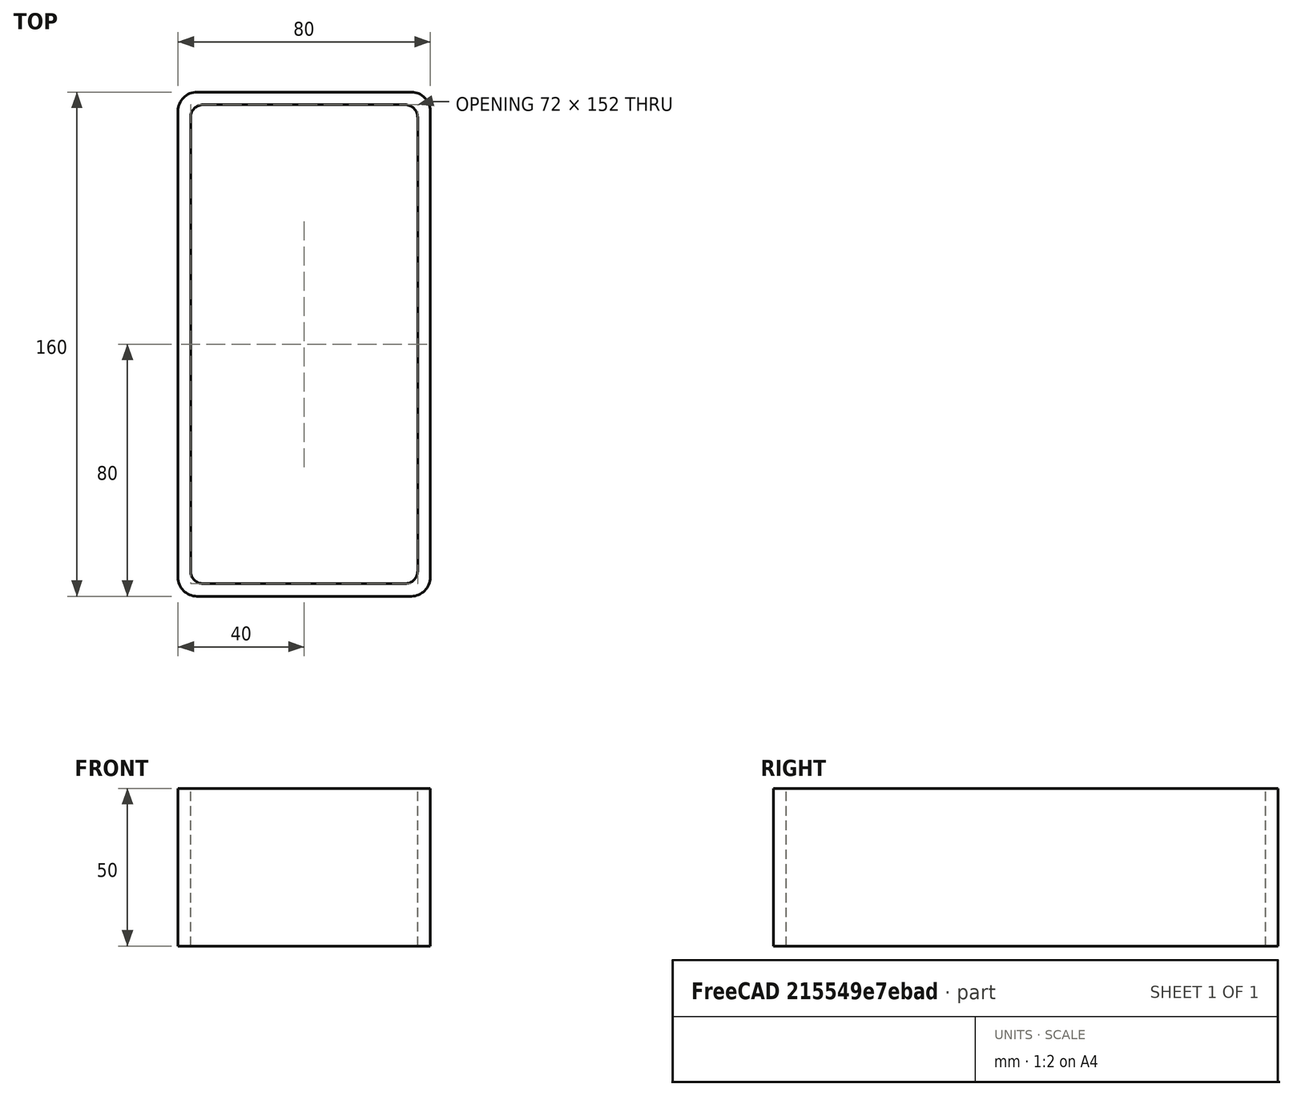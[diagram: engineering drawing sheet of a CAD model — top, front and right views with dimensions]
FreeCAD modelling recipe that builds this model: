
FCSTD DOCUMENT  (FreeCAD 0.15R4671 (Git))
Label: Rectangular hollow section 160x80x4 EN10219 S235JRH
License: All rights reserved
LicenseURL: http://en.wikipedia.org/wiki/All_rights_reserved
objects: Sketcher::SketchObject×1, Part::Extrusion×1
note: 2 computed .brp shape members not serialized (recipe doc carries the construction recipe); baked Part::Feature solids carry a one-line shape summary decoded from their .brp

FEATURE [Sketcher::SketchObject] Sketch
  sketch-geometry (16):
    g0: LineSegment StartX=-32 StartY=76 StartZ=0 EndX=32 EndY=76 EndZ=0
    g1: LineSegment StartX=36 StartY=72 StartZ=0 EndX=36 EndY=-72 EndZ=0
    g2: LineSegment StartX=32 StartY=-76 StartZ=0 EndX=-32 EndY=-76 EndZ=0
    g3: LineSegment StartX=-36 StartY=-72 StartZ=0 EndX=-36 EndY=72 EndZ=0
    g4: LineSegment StartX=-34 StartY=80 StartZ=0 EndX=34 EndY=80 EndZ=0
    g5: LineSegment StartX=40 StartY=74 StartZ=0 EndX=40 EndY=-74 EndZ=0
    g6: LineSegment StartX=34 StartY=-80 StartZ=0 EndX=-34 EndY=-80 EndZ=0
    g7: LineSegment StartX=-40 StartY=-74 StartZ=0 EndX=-40 EndY=74 EndZ=0
    g8: ArcOfCircle CenterX=-32 CenterY=72 CenterZ=0 NormalX=0 NormalY=0 NormalZ=1 Radius=4 StartAngle=1.5708 EndAngle=3.14159
    g9: ArcOfCircle CenterX=32 CenterY=72 CenterZ=0 NormalX=0 NormalY=0 NormalZ=1 Radius=4 StartAngle=0 EndAngle=1.5708
    g10: ArcOfCircle CenterX=32 CenterY=-72 CenterZ=0 NormalX=0 NormalY=0 NormalZ=1 Radius=4 StartAngle=4.71239 EndAngle=6.28319
    g11: ArcOfCircle CenterX=-32 CenterY=-72 CenterZ=0 NormalX=0 NormalY=0 NormalZ=1 Radius=4 StartAngle=3.14159 EndAngle=4.71239
    g12: ArcOfCircle CenterX=34 CenterY=74 CenterZ=0 NormalX=0 NormalY=0 NormalZ=1 Radius=6 StartAngle=0 EndAngle=1.5708
    g13: ArcOfCircle CenterX=34 CenterY=-74 CenterZ=0 NormalX=0 NormalY=0 NormalZ=1 Radius=6 StartAngle=4.71239 EndAngle=6.28319
    g14: ArcOfCircle CenterX=-34 CenterY=-74 CenterZ=0 NormalX=0 NormalY=0 NormalZ=1 Radius=6 StartAngle=3.14159 EndAngle=4.71239
    g15: ArcOfCircle CenterX=-34 CenterY=74 CenterZ=0 NormalX=0 NormalY=0 NormalZ=1 Radius=6 StartAngle=1.5708 EndAngle=3.14159
  constraints (36):
    c: Horizontal(g2)
    c: Vertical(g3)
    c: Horizontal(g6)
    c: Vertical(g7)
    c: Tangent(g3,g8) = 1.5708
    c: Tangent(g0,g8) = 1.5708
    c: Tangent(g0,g9) = 1.5708
    c: Tangent(g1,g9) = 1.5708
    c: Tangent(g1,g10) = 1.5708
    c: Tangent(g2,g10) = 1.5708
    c: Tangent(g2,g11) = 1.5708
    c: Tangent(g3,g11) = 1.5708
    c: Tangent(g4,g12) = 1.5708
    c: Tangent(g5,g12) = 1.5708
    c: Tangent(g5,g13) = 1.5708
    c: Tangent(g6,g13) = 1.5708
    c: Tangent(g6,g14) = 1.5708
    c: Tangent(g7,g14) = 1.5708
    c: Tangent(g7,g15) = 1.5708
    c: Tangent(g4,g15) = 1.5708
    c: Equal(g9,g8)
    c: Equal(g9,g11)
    c: Equal(g9,g10)
    c: Equal(g12,g15)
    c: Equal(g12,g14)
    c: Equal(g12,g13)
    c: Symmetric(g4,g6,g-1)
    c: Symmetric(g7,g5,g-2)
    c: DistanceY(g4,g6) = -160
    c: DistanceX(g7,g5) = 80
    c: Symmetric(g3,g1,g-2)
    c: Symmetric(g0,g2,g-1)
    c: DistanceY(g0,g4) = 4
    c: DistanceX(g5,g1) = -4
    c: Radius(g9) = 4
    c: Radius(g12) = 6
FEATURE [Part::Extrusion] Extrude  label="Rectangular hollow section 160x80x4 EN10219 S235JRH"
  Base = -> Sketch
  Dir = (0,0,50)
  Solid = true
